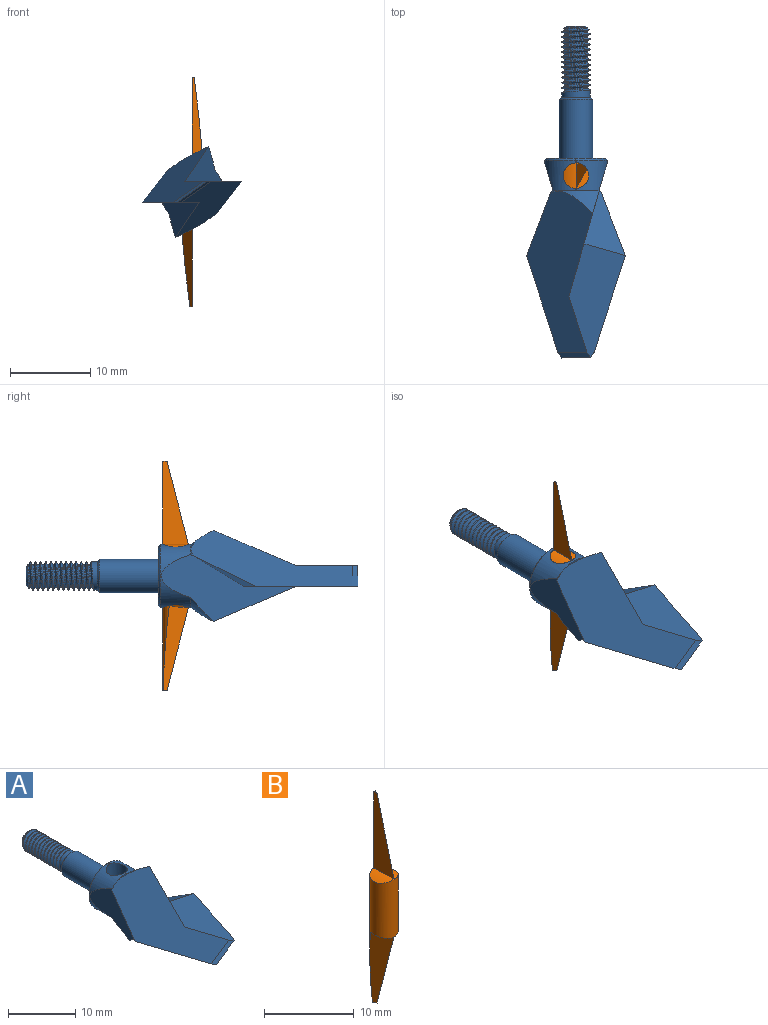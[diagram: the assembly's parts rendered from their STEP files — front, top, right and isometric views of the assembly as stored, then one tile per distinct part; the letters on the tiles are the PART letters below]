
ASSEMBLY  parts=2 mates=1
PART A: 49 faces, bbox 12.3x275.8x12.1 mm
  f0: cylinder r=2.08mm len=7.37mm, axis (0,-1,0), area 96.4mm2, adj f2,f36
  f1: plane 3.66x3.66mm, normal (0,1,0), area 0.9mm2, adj f2,f3
  f2: cone r=2.08mm half-angle=45deg, axis (0,-1,0), area 4.4mm2, adj f0,f1
  f3: cylinder r=1.75mm len=3.51mm, axis (0,-1,0), area 7.4mm2, adj f1,f4,f18,f20,f21
  f4: cylinder r=1.75mm len=3.51mm, axis (0,-1,0), area 1mm2, adj f3,f5,f20,f21
  f5: cylinder r=1.75mm len=3.51mm, axis (0,-1,0), area 1mm2, adj f4,f6,f20,f21
  f6: cylinder r=1.75mm len=3.51mm, axis (0,-1,0), area 1mm2, adj f5,f7,f20,f21
  f7: cylinder r=1.75mm len=3.51mm, axis (0,-1,0), area 1mm2, adj f6,f8,f20,f21
  f8: cylinder r=1.75mm len=3.51mm, axis (0,-1,0), area 1mm2, adj f7,f9,f20,f21
  f9: cylinder r=1.75mm len=3.51mm, axis (0,-1,0), area 1mm2, adj f8,f10,f20,f21
  f10: cylinder r=1.75mm len=3.51mm, axis (0,-1,0), area 1mm2, adj f9,f11,f20,f21
  f11: cylinder r=1.75mm len=3.51mm, axis (0,-1,0), area 1mm2, adj f10,f12,f20,f21
  f12: cylinder r=1.75mm len=3.51mm, axis (0,-1,0), area 1mm2, adj f11,f13,f20,f21
  f13: cylinder r=1.75mm len=3.51mm, axis (0,-1,0), area 1mm2, adj f12,f14,f20,f21
  f14: cylinder r=1.75mm len=3.51mm, axis (0,-1,0), area 1mm2, adj f13,f15,f20,f21
  f15: cylinder r=1.75mm len=1.33mm, axis (0,-1,0), area 0.1mm2, adj f14,f17,f20
  f16: plane 2.49x2.49mm, normal (0,1,0), area 4.9mm2, adj f17
  f17: cone r=1.24mm half-angle=45deg, axis (0,-1,0), area 4mm2, adj f15,f16,f19,f20,f21
  f18: plane 0.55x0.35mm, normal (0,0,-1), area 0.1mm2, adj f3,f19,f20,f21
  f19: cylinder r=1.4mm len=8.24mm, axis (0,1,0), area 16.6mm2, adj f17,f18,f20,f21
  f20: bspline ~8.35x4.05mm, area 49.1mm2, adj f3,f4,f5,f6,f7,f8,f9,f10
  f21: bspline ~8.46x4.05mm, area 51.4mm2, adj f3,f4,f5,f6,f7,f8,f9,f10
  f22: plane 5.77x1.26mm, normal (0,1,0), area 0mm2, adj f24,f31,f34,f35,f43,f44,f48
  f23: plane 5.77x1.26mm, normal (0,1,0), area 0mm2, adj f24,f32,f33,f35,f45,f46,f47
  f24: cylinder r=3.94mm len=7.87mm, axis (0,1,0), area 24.6mm2, adj f22,f23,f31,f33,f37,f38,f39,f42
  f25: plane 14.25x7.04mm, normal (0,0,-1), area 54.3mm2, adj f27,f28,f29,f30,f32,f34
  f26: plane 14.25x7.04mm, normal (0,0,1), area 54.3mm2, adj f27,f28,f29,f30,f31,f33
  f27: plane 4.07x2.54mm, normal (0.54,-0.34,-0.77), area 3.3mm2, adj f25,f26,f28,f29
  f28: plane 4.07x2.54mm, normal (-0.54,-0.34,0.77), area 3.3mm2, adj f25,f26,f27,f30
  f29: plane 20.09x8.23mm, normal (0.56,-0.18,-0.81), area 120.3mm2, adj f25,f26,f27,f32,f33,f47
  f30: plane 20.09x8.23mm, normal (-0.56,-0.18,0.81), area 120.3mm2, adj f25,f26,f28,f31,f34,f48
  f31: plane 16.82x8.36mm, normal (0.96,-0.28,0), area 60.1mm2, adj f22,f24,f26,f30,f33,f48
  f32: plane 16.82x8.36mm, normal (-0.96,-0.28,0), area 60.1mm2, adj f23,f25,f29,f34,f35,f47
  f33: plane 8.07x5.17mm, normal (0.14,0.48,0.87), area 22.1mm2, adj f23,f24,f26,f29,f31,f47
  f34: plane 8.07x5.17mm, normal (-0.14,0.48,-0.87), area 22.1mm2, adj f22,f25,f30,f32,f35,f48
  f35: cylinder r=3.94mm len=7.87mm, axis (0,1,0), area 24.6mm2, adj f22,f23,f32,f34,f37,f38,f40,f41
  f36: plane 7.37x7.37mm, normal (0,1,0), area 29mm2, adj f0,f38
  f37: cylinder r=1.59mm len=7.87mm, axis (0,0,1), area 75.2mm2, adj f24,f35,f39,f40,f41,f42,f43,f44
  f38: cone r=3.94mm half-angle=45deg, axis (0,-1,0), area 8.6mm2, adj f24,f35,f36,f39,f40,f41,f42
  f39: bspline ~259.18x0.32mm, area 0mm2, adj f24,f37,f38,f40
  f40: bspline ~259.18x0.33mm, area 0mm2, adj f35,f37,f38,f39
  f41: bspline ~259.18x0.32mm, area 0mm2, adj f35,f37,f38,f42
  f42: bspline ~259.18x0.33mm, area 0mm2, adj f24,f37,f38,f41
  f43: bspline ~259.18x0.33mm, area 0mm2, adj f22,f35,f37,f44
  f44: bspline ~259.18x0.32mm, area 0mm2, adj f22,f24,f37,f43
  f45: bspline ~259.18x0.33mm, area 0mm2, adj f23,f24,f37,f46
  f46: bspline ~259.18x0.32mm, area 0mm2, adj f23,f35,f37,f45
  f47: cone r=6.48mm half-angle=36.5deg, axis (0,-1,0), area 7.8mm2, adj f23,f29,f32,f33
  f48: cone r=6.48mm half-angle=36.5deg, axis (0,-1,0), area 7.8mm2, adj f22,f30,f31,f34
PART B: 11 faces, bbox 3.2x3.2x28.6 mm
  f0: cylinder r=1.59mm len=28.58mm, axis (0,0,-1), area 94.9mm2, adj f1,f2,f3,f4,f5,f6,f7,f8
  f1: plane 0.51x0.27mm, normal (0,0,-1), area 0.1mm2, adj f0,f6,f9
  f2: plane 0.51x0.27mm, normal (0,0,1), area 0.1mm2, adj f0,f4,f7
  f3: cylinder r=3.94mm len=3.18mm, axis (0,1,0), area 4mm2, adj f0,f4
  f4: plane 10.35x3.18mm, normal (-1,0,0), area 19.1mm2, adj f0,f2,f3,f7
  f5: cylinder r=3.94mm len=3.18mm, axis (0,1,0), area 4mm2, adj f0,f6
  f6: plane 10.35x3.18mm, normal (1,0,0), area 19.1mm2, adj f0,f1,f5,f9
  f7: plane 10.66x3.22mm, normal (0.87,-0.48,0.12), area 18.6mm2, adj f0,f2,f4,f8
  f8: cylinder r=3.94mm len=2.39mm, axis (0,1,0), area 1.6mm2, adj f0,f7
  f9: plane 10.67x3.22mm, normal (-0.87,-0.48,-0.12), area 18.6mm2, adj f0,f1,f6,f10
  f10: cylinder r=3.94mm len=2.39mm, axis (0,1,0), area 1.6mm2, adj f0,f9
PLACE A at identity fixed
PLACE B t=(0,-2.16,0)mm
MATE cylindrical A.f37 <-> B.f0  axis (0,0,1) through (0,-2.16,0)mm
